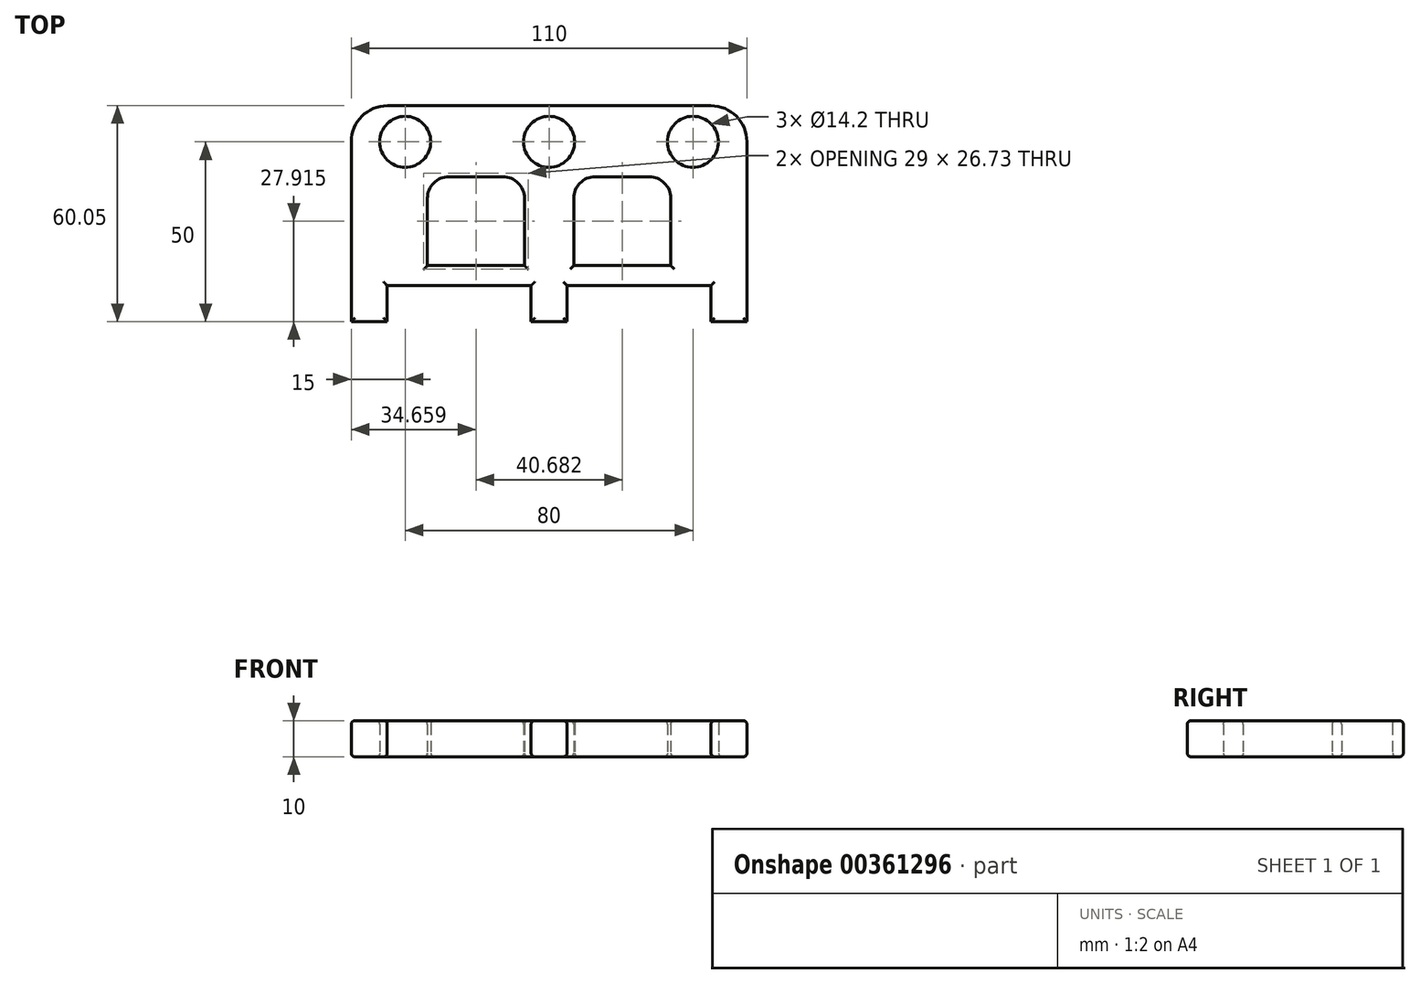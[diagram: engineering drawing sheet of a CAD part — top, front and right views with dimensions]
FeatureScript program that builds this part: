
annotation { "Feature Type Name" : "Feature", "Feature Type Description" : "" }
export const myFeature = defineFeature(function(context is Context, id is Id, definition is map)
    precondition{}
    {
        {
            var Q0;
            Q0=qCreatedBy(makeId("Top.planeOp"),FACE);
            var sketch = newSketch(context, id + "F0", { "sketchPlane" : qUnion([Q0])});
            skCircle(sketch, "E0", {"center": v(0, 0) * mm, "radius": 7.1 * mm});
            skCircle(sketch, "E1", {"center": v(0, 0) * mm, "radius": 40 * mm, "construction": true});
            skCircle(sketch, "E2", {"center": v(-40, 0) * mm, "radius": 7.1 * mm});
            skCircle(sketch, "E3", {"center": v(40, 0) * mm, "radius": 7.1 * mm});
            skLineSegment(sketch, "E4", {"start": v(-45, -40) * mm, "end": v(-5, -40) * mm});
            skLineSegment(sketch, "E5", {"start": v(-55, -40) * mm, "end": v(-55, 0) * mm});
            skLineSegment(sketch, "E6", {"start": v(55, -40) * mm, "end": v(55, 0) * mm});
            skLineSegment(sketch, "E7.top", {"start": v(-55, -50) * mm, "end": v(-45, -50) * mm});
            skLineSegment(sketch, "E7.left", {"start": v(-55, -40) * mm, "end": v(-55, -50) * mm});
            skLineSegment(sketch, "E7.right", {"start": v(-45, -40) * mm, "end": v(-45, -50) * mm});
            skLineSegment(sketch, "E8.top", {"start": v(55, -50) * mm, "end": v(45, -50) * mm});
            skLineSegment(sketch, "E8.left", {"start": v(55, -40) * mm, "end": v(55, -50) * mm});
            skLineSegment(sketch, "E8.right", {"start": v(45, -40) * mm, "end": v(45, -50) * mm});
            skLineSegment(sketch, "E9.top", {"start": v(0, -50) * mm, "end": v(-5, -50) * mm});
            skLineSegment(sketch, "E9.left", {"start": v(0, -40) * mm, "end": v(0, -50) * mm});
            skLineSegment(sketch, "E9.right", {"start": v(-5, -40) * mm, "end": v(-5, -50) * mm});
            skLineSegment(sketch, "E10.top", {"start": v(0, -50) * mm, "end": v(5, -50) * mm});
            skLineSegment(sketch, "E10.right", {"start": v(5, -40) * mm, "end": v(5, -50) * mm});
            skLineSegment(sketch, "E11.trimOffspring", {"start": v(5, -40) * mm, "end": v(45, -40) * mm});
            skLineSegment(sketch, "E12", {"start": v(-44.95, 10.05) * mm, "end": v(44.95, 10.05) * mm});
            skCircle(sketch, "E13", {"center": v(-55, 0) * mm, "radius": 10.05 * mm, "construction": true});
            skCircle(sketch, "E14", {"center": v(55, 0) * mm, "radius": 10.05 * mm, "construction": true});
            skArc(sketch, "E15", {"start": v(-44.95, 10.05) * mm, "mid": v(-52.06, 7.1) * mm, "end": v(-55, 0) * mm});
            skArc(sketch, "E16", {"start": v(55, 0) * mm, "mid": v(52.06, 7.1) * mm, "end": v(44.95, 10.05) * mm});
            skLineSegment(sketch, "E17.bottom", {"start": v(-6.84, -34.45) * mm, "end": v(-33.84, -34.45) * mm});
            skLineSegment(sketch, "E17.top", {"start": v(-12.84, -9.72) * mm, "end": v(-27.84, -9.72) * mm});
            skLineSegment(sketch, "E17.left", {"start": v(-6.84, -34.45) * mm, "end": v(-6.84, -15.72) * mm});
            skLineSegment(sketch, "E17.right", {"start": v(-33.84, -34.45) * mm, "end": v(-33.84, -15.72) * mm});
            skPoint(sketch, "E18.visualSharp", {"position": v(-33.84, -9.72) * mm});
            skArc(sketch, "E18.filletArc", {"start": v(-27.84, -9.72) * mm, "mid": v(-32.09, -11.48) * mm, "end": v(-33.84, -15.72) * mm});
            skPoint(sketch, "E19.visualSharp", {"position": v(-6.84, -9.72) * mm});
            skArc(sketch, "E19.filletArc", {"start": v(-6.84, -15.72) * mm, "mid": v(-8.6, -11.48) * mm, "end": v(-12.84, -9.72) * mm});
            skArc(sketch, "E20.MirrorCS", {"start": v(6.84, -15.72) * mm, "mid": v(8.6, -11.48) * mm, "end": v(12.84, -9.72) * mm});
            skLineSegment(sketch, "E21.MirrorCS", {"start": v(6.84, -34.45) * mm, "end": v(6.84, -15.72) * mm});
            skLineSegment(sketch, "E22.MirrorCS", {"start": v(6.84, -34.45) * mm, "end": v(33.84, -34.45) * mm});
            skLineSegment(sketch, "E23.MirrorCS", {"start": v(12.84, -9.72) * mm, "end": v(27.84, -9.72) * mm});
            skLineSegment(sketch, "E24.MirrorCS", {"start": v(33.84, -34.45) * mm, "end": v(33.84, -15.72) * mm});
            skArc(sketch, "E25.MirrorCS", {"start": v(27.84, -9.72) * mm, "mid": v(32.09, -11.48) * mm, "end": v(33.84, -15.72) * mm});
            skSolve(sketch);
        }
        {
            var Q0;
            Q0=makeQuery(id+"F0.imprint","IMPRINT",FACE,{"disambiguationData":[TD([[makeQuery(id+"F0.imprint","IMPRINT",EDGE,{"derivedFrom":sQuery(id+"F0.wireOp",EDGE,"E0")}),-1.0]])]});
            extrude(context, id + "F1", {"entities" : qUnion([Q0]), "endBound" : BoundingType.SYMMETRIC, "depth" : 10 * mm});
        }
        {
            var Q0;
            Q0=makeQuery(id+"F1.opExtrude","CAP_FACE",FACE,{"disambiguationData":[OSD([sQuery(id+"F0.wireOp",EDGE,"E0"),sQuery(id+"F0.wireOp",EDGE,"E2"),sQuery(id+"F0.wireOp",EDGE,"E3"),sQuery(id+"F0.wireOp",EDGE,"E4"),sQuery(id+"F0.wireOp",EDGE,"E5"),sQuery(id+"F0.wireOp",EDGE,"E6"),sQuery(id+"F0.wireOp",EDGE,"E7.top"),sQuery(id+"F0.wireOp",EDGE,"E7.left"),sQuery(id+"F0.wireOp",EDGE,"E7.right"),sQuery(id+"F0.wireOp",EDGE,"E8.top"),sQuery(id+"F0.wireOp",EDGE,"E8.left"),sQuery(id+"F0.wireOp",EDGE,"E8.right"),sQuery(id+"F0.wireOp",EDGE,"E9.top"),sQuery(id+"F0.wireOp",EDGE,"E9.right"),sQuery(id+"F0.wireOp",EDGE,"E10.top"),sQuery(id+"F0.wireOp",EDGE,"E10.right"),sQuery(id+"F0.wireOp",EDGE,"E11.trimOffspring"),sQuery(id+"F0.wireOp",EDGE,"E12"),sQuery(id+"F0.wireOp",EDGE,"E15"),sQuery(id+"F0.wireOp",EDGE,"E16"),sQuery(id+"F0.wireOp",EDGE,"E17.bottom"),sQuery(id+"F0.wireOp",EDGE,"E17.top"),sQuery(id+"F0.wireOp",EDGE,"E17.left"),sQuery(id+"F0.wireOp",EDGE,"E17.right"),sQuery(id+"F0.wireOp",EDGE,"E18.filletArc"),sQuery(id+"F0.wireOp",EDGE,"E19.filletArc"),sQuery(id+"F0.wireOp",EDGE,"E20.MirrorCS"),sQuery(id+"F0.wireOp",EDGE,"E21.MirrorCS"),sQuery(id+"F0.wireOp",EDGE,"E22.MirrorCS"),sQuery(id+"F0.wireOp",EDGE,"E23.MirrorCS"),sQuery(id+"F0.wireOp",EDGE,"E24.MirrorCS"),sQuery(id+"F0.wireOp",EDGE,"E25.MirrorCS")])],"isStart":false});
            var Q1;
            Q1=makeQuery(id+"F1.opExtrude","CAP_FACE",FACE,{"disambiguationData":[OSD([sQuery(id+"F0.wireOp",EDGE,"E0"),sQuery(id+"F0.wireOp",EDGE,"E2"),sQuery(id+"F0.wireOp",EDGE,"E3"),sQuery(id+"F0.wireOp",EDGE,"E4"),sQuery(id+"F0.wireOp",EDGE,"E5"),sQuery(id+"F0.wireOp",EDGE,"E6"),sQuery(id+"F0.wireOp",EDGE,"E7.top"),sQuery(id+"F0.wireOp",EDGE,"E7.left"),sQuery(id+"F0.wireOp",EDGE,"E7.right"),sQuery(id+"F0.wireOp",EDGE,"E8.top"),sQuery(id+"F0.wireOp",EDGE,"E8.left"),sQuery(id+"F0.wireOp",EDGE,"E8.right"),sQuery(id+"F0.wireOp",EDGE,"E9.top"),sQuery(id+"F0.wireOp",EDGE,"E9.right"),sQuery(id+"F0.wireOp",EDGE,"E10.top"),sQuery(id+"F0.wireOp",EDGE,"E10.right"),sQuery(id+"F0.wireOp",EDGE,"E11.trimOffspring"),sQuery(id+"F0.wireOp",EDGE,"E12"),sQuery(id+"F0.wireOp",EDGE,"E15"),sQuery(id+"F0.wireOp",EDGE,"E16"),sQuery(id+"F0.wireOp",EDGE,"E17.bottom"),sQuery(id+"F0.wireOp",EDGE,"E17.top"),sQuery(id+"F0.wireOp",EDGE,"E17.left"),sQuery(id+"F0.wireOp",EDGE,"E17.right"),sQuery(id+"F0.wireOp",EDGE,"E18.filletArc"),sQuery(id+"F0.wireOp",EDGE,"E19.filletArc"),sQuery(id+"F0.wireOp",EDGE,"E20.MirrorCS"),sQuery(id+"F0.wireOp",EDGE,"E21.MirrorCS"),sQuery(id+"F0.wireOp",EDGE,"E22.MirrorCS"),sQuery(id+"F0.wireOp",EDGE,"E23.MirrorCS"),sQuery(id+"F0.wireOp",EDGE,"E24.MirrorCS"),sQuery(id+"F0.wireOp",EDGE,"E25.MirrorCS")])],"isStart":true});
            fillet(context, id + "F2", {"entities" : qUnion([Q0, Q1]), "radius" : 1 * mm, "tangentPropagation" : true, "allowEdgeOverflow" : false});
        }
    });
